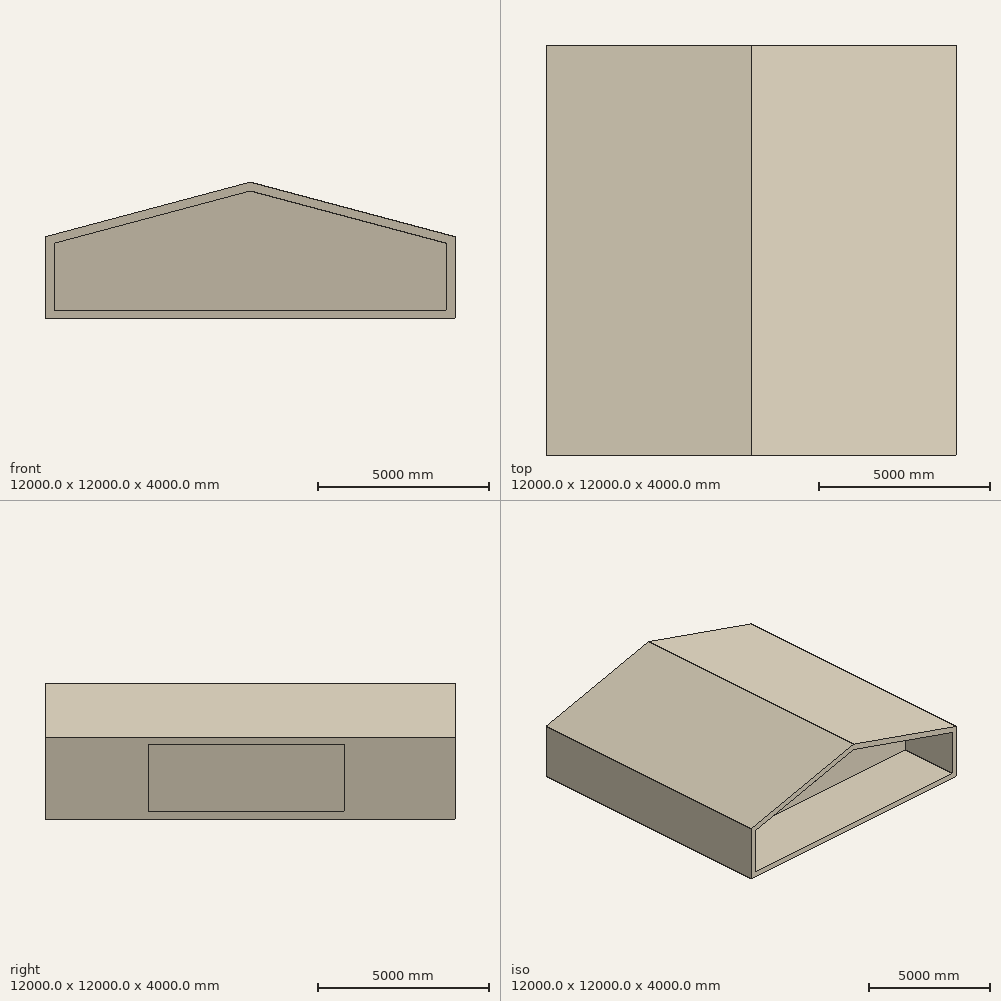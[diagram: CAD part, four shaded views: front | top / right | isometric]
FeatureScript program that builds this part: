
annotation { "Feature Type Name" : "Feature", "Feature Type Description" : "" }
export const myFeature = defineFeature(function(context is Context, id is Id, definition is map)
    precondition{}
    {
        {
            var Q0;
            Q0=qCreatedBy(makeId("Front.planeOp"),FACE);
            var sketch = newSketch(context, id + "F0", { "sketchPlane" : qUnion([Q0])});
            skLineSegment(sketch, "E0", {"start": v(0, 0) * mm, "end": v(6000, 1600) * mm});
            skLineSegment(sketch, "E1", {"start": v(6000, 1600) * mm, "end": v(12000, 0) * mm});
            skLineSegment(sketch, "E2", {"start": v(12000, 0) * mm, "end": v(12000, -2400) * mm});
            skLineSegment(sketch, "E3", {"start": v(12000, -2400) * mm, "end": v(0, -2400) * mm});
            skLineSegment(sketch, "E4", {"start": v(0, -2400) * mm, "end": v(0, 0) * mm});
            skLineSegment(sketch, "E5.0", {"start": v(6000, 1341.26) * mm, "end": v(11750, -192.07) * mm});
            skLineSegment(sketch, "E5.1", {"start": v(250, -192.07) * mm, "end": v(6000, 1341.26) * mm});
            skLineSegment(sketch, "E5.2", {"start": v(11750, -192.07) * mm, "end": v(11750, -2150) * mm});
            skLineSegment(sketch, "E5.3", {"start": v(11750, -2150) * mm, "end": v(250, -2150) * mm});
            skLineSegment(sketch, "E5.4", {"start": v(250, -2150) * mm, "end": v(250, -192.07) * mm});
            skSolve(sketch);
        }
        {
            var Q0;
            Q0=makeQuery(id+"F0.imprint","IMPRINT",FACE,{"disambiguationData":[TD([[makeQuery(id+"F0.imprint","IMPRINT",EDGE,{"derivedFrom":sQuery(id+"F0.wireOp",EDGE,"E0")}),-1.0]])]});
            extrude(context, id + "F1", {"entities" : qUnion([Q0]), "depth" : 12000 * mm});
        }
        {
            var Q0;
            Q0=qCreatedBy(makeId("Front.planeOp"),FACE);
            cPlane(context, id + "F2", {"entities" : qUnion([Q0]), "cplaneType" : CPlaneType.OFFSET, "offset" : 3000 * mm, "width" : 150 * mm, "height" : 150 * mm});
        }
        {
            var Q0;
            Q0=qCreatedBy(id+"F2.planeOp",FACE);
            var sketch = newSketch(context, id + "F3", { "sketchPlane" : qUnion([Q0])});
            skLineSegment(sketch, "E6.0", {"start": v(6000, 1341.26) * mm, "end": v(11750, -192.07) * mm});
            skLineSegment(sketch, "E7.0", {"start": v(11750, -192.07) * mm, "end": v(11750, -2150) * mm});
            skLineSegment(sketch, "E8.0", {"start": v(11750, -2150) * mm, "end": v(250, -2150) * mm});
            skLineSegment(sketch, "E9.0", {"start": v(250, -2150) * mm, "end": v(250, -192.07) * mm});
            skLineSegment(sketch, "E10.0", {"start": v(250, -192.07) * mm, "end": v(6000, 1341.26) * mm});
            skSolve(sketch);
        }
        {
            var Q0;
            Q0 = qSketchRegion(id + "F3", true);
            extrude(context, id + "F4", {"entities" : qUnion([Q0]), "operationType" : NewBodyOperationType.ADD, "depth" : 250 * mm});
        }
        {
            var Q0;
            Q0=qCreatedBy(id+"F2.planeOp",FACE);
            cPlane(context, id + "F5", {"entities" : qUnion([Q0]), "cplaneType" : CPlaneType.OFFSET, "offset" : 6000 * mm, "width" : 150 * mm, "height" : 150 * mm});
        }
        {
            var Q0;
            Q0=qCreatedBy(id+"F5.planeOp",FACE);
            var sketch = newSketch(context, id + "F6", { "sketchPlane" : qUnion([Q0])});
            skLineSegment(sketch, "E11.0", {"start": v(11750, -2150) * mm, "end": v(250, -2150) * mm});
            skLineSegment(sketch, "E12.0", {"start": v(11750, -192.07) * mm, "end": v(11750, -2150) * mm});
            skLineSegment(sketch, "E13.0", {"start": v(250, -2150) * mm, "end": v(250, -192.07) * mm});
            skLineSegment(sketch, "E14.0", {"start": v(250, -192.07) * mm, "end": v(6000, 1341.26) * mm});
            skLineSegment(sketch, "E15.0", {"start": v(6000, 1341.26) * mm, "end": v(11750, -192.07) * mm});
            skSolve(sketch);
        }
        {
            var Q0;
            Q0 = qSketchRegion(id + "F6", true);
            extrude(context, id + "F7", {"entities" : qUnion([Q0]), "depth" : 250 * mm});
        }
        {
            var Q0;
            {var subQ1=sQuery(id+"F0.wireOp",EDGE,"E5.3");Q0=makeQuery(id+"F4.boolean.opBoolean","SPLIT",FACE,{"disambiguationData":[TD([makeQuery(id+"F4.opExtrude","CAP_FACE",FACE,{"disambiguationData":[OSD([sQuery(id+"F3.wireOp",EDGE,"E6.0"),sQuery(id+"F3.wireOp",EDGE,"E7.0"),sQuery(id+"F3.wireOp",EDGE,"E8.0"),sQuery(id+"F3.wireOp",EDGE,"E9.0"),sQuery(id+"F3.wireOp",EDGE,"E10.0")])],"isStart":true})])],"derivedFrom":makeQuery(id+"F1.opExtrude","SWEPT_FACE",FACE,{"disambiguationData":[OSD([subQ1])]})});}
            var sketch = newSketch(context, id + "F8", { "sketchPlane" : qUnion([Q0])});
            skLineSegment(sketch, "E16.bottom", {"start": v(5867.2, -3250) * mm, "end": v(6117.2, -3250) * mm});
            skLineSegment(sketch, "E16.top", {"start": v(5867.2, -9000) * mm, "end": v(6117.2, -9000) * mm});
            skLineSegment(sketch, "E16.left", {"start": v(5867.2, -3250) * mm, "end": v(5867.2, -9000) * mm});
            skLineSegment(sketch, "E16.right", {"start": v(6117.2, -3250) * mm, "end": v(6117.2, -9000) * mm});
            skSolve(sketch);
        }
        {
            var Q0;
            Q0 = qSketchRegion(id + "F8", true);
            extrude(context, id + "F9", {"entities" : qUnion([Q0]), "endBound" : BoundingType.UP_TO_NEXT, "depth" : 25 * mm});
        }
        {
            var Q0;
            Q0=makeQuery(id+"F1.opExtrude","SWEPT_FACE",FACE,{"disambiguationData":[OSD([sQuery(id+"F0.wireOp",EDGE,"E2")])]});
            var sketch = newSketch(context, id + "F10", { "sketchPlane" : qUnion([Q0])});
            skLineSegment(sketch, "E17.0", {"start": v(-9000, -192.07) * mm, "end": v(-9000, -2150) * mm});
            skLineSegment(sketch, "E18.0", {"start": v(-12000, -192.07) * mm, "end": v(-3250, -192.07) * mm});
            skLineSegment(sketch, "E19.0", {"start": v(-3250, -192.07) * mm, "end": v(-3250, -2150) * mm});
            skLineSegment(sketch, "E20.0", {"start": v(-12000, -2150) * mm, "end": v(-3250, -2150) * mm});
            skSolve(sketch);
        }
        {
            var Q0;
            Q0 = qSketchRegion(id + "F10", true);
            extrude(context, id + "F11", {"entities" : qUnion([Q0]), "operationType" : NewBodyOperationType.REMOVE, "oppositeDirection" : true, "depth" : 250 * mm});
        }
        {
            var Q0;
            Q0=makeQuery(id+"F7.opExtrude","CAP_FACE",FACE,{"disambiguationData":[OSD([sQuery(id+"F6.wireOp",EDGE,"E11.0"),sQuery(id+"F6.wireOp",EDGE,"E12.0"),sQuery(id+"F6.wireOp",EDGE,"E13.0"),sQuery(id+"F6.wireOp",EDGE,"E14.0"),sQuery(id+"F6.wireOp",EDGE,"E15.0")])],"isStart":true});
            var sketch = newSketch(context, id + "F12", { "sketchPlane" : qUnion([Q0])});
            skLineSegment(sketch, "E21.bottom", {"start": v(-11750, -192.07) * mm, "end": v(-9350, -192.07) * mm});
            skLineSegment(sketch, "E21.top", {"start": v(-11750, -1392.07) * mm, "end": v(-9350, -1392.07) * mm});
            skLineSegment(sketch, "E21.left", {"start": v(-11750, -192.07) * mm, "end": v(-11750, -1392.07) * mm});
            skLineSegment(sketch, "E21.right", {"start": v(-9350, -192.07) * mm, "end": v(-9350, -1392.07) * mm});
            skLineSegment(sketch, "E22.MirrorCS", {"start": v(-11750, 1007.93) * mm, "end": v(-9350, 1007.93) * mm});
            skLineSegment(sketch, "E23.MirrorCS", {"start": v(-9350, -192.07) * mm, "end": v(-9350, 1007.93) * mm});
            skSolve(sketch);
        }
        {
            var Q0;
            Q0 = qSketchRegion(id + "F12", true);
            extrude(context, id + "F13", {"entities" : qUnion([Q0]), "operationType" : NewBodyOperationType.REMOVE, "oppositeDirection" : true, "depth" : 200 * mm});
        }
        {
            var Q0;
            Q0=makeQuery(id+"F7.opExtrude","CAP_FACE",FACE,{"disambiguationData":[OSD([sQuery(id+"F6.wireOp",EDGE,"E11.0"),sQuery(id+"F6.wireOp",EDGE,"E12.0"),sQuery(id+"F6.wireOp",EDGE,"E13.0"),sQuery(id+"F6.wireOp",EDGE,"E14.0"),sQuery(id+"F6.wireOp",EDGE,"E15.0")])],"isStart":true});
            var sketch = newSketch(context, id + "F14", { "sketchPlane" : qUnion([Q0])});
            skLineSegment(sketch, "E24.bottom", {"start": v(-7317.2, -192.07) * mm, "end": v(-6117.2, -192.07) * mm});
            skLineSegment(sketch, "E24.top", {"start": v(-7317.2, -1942.07) * mm, "end": v(-6117.2, -1942.07) * mm});
            skLineSegment(sketch, "E24.left", {"start": v(-7317.2, -192.07) * mm, "end": v(-7317.2, -1942.07) * mm});
            skLineSegment(sketch, "E24.right", {"start": v(-6117.2, -192.07) * mm, "end": v(-6117.2, -1942.07) * mm});
            skSolve(sketch);
        }
        {
            var Q0;
            Q0 = qSketchRegion(id + "F14", true);
            extrude(context, id + "F15", {"entities" : qUnion([Q0]), "operationType" : NewBodyOperationType.REMOVE, "oppositeDirection" : true, "depth" : 200 * mm});
        }
    });
